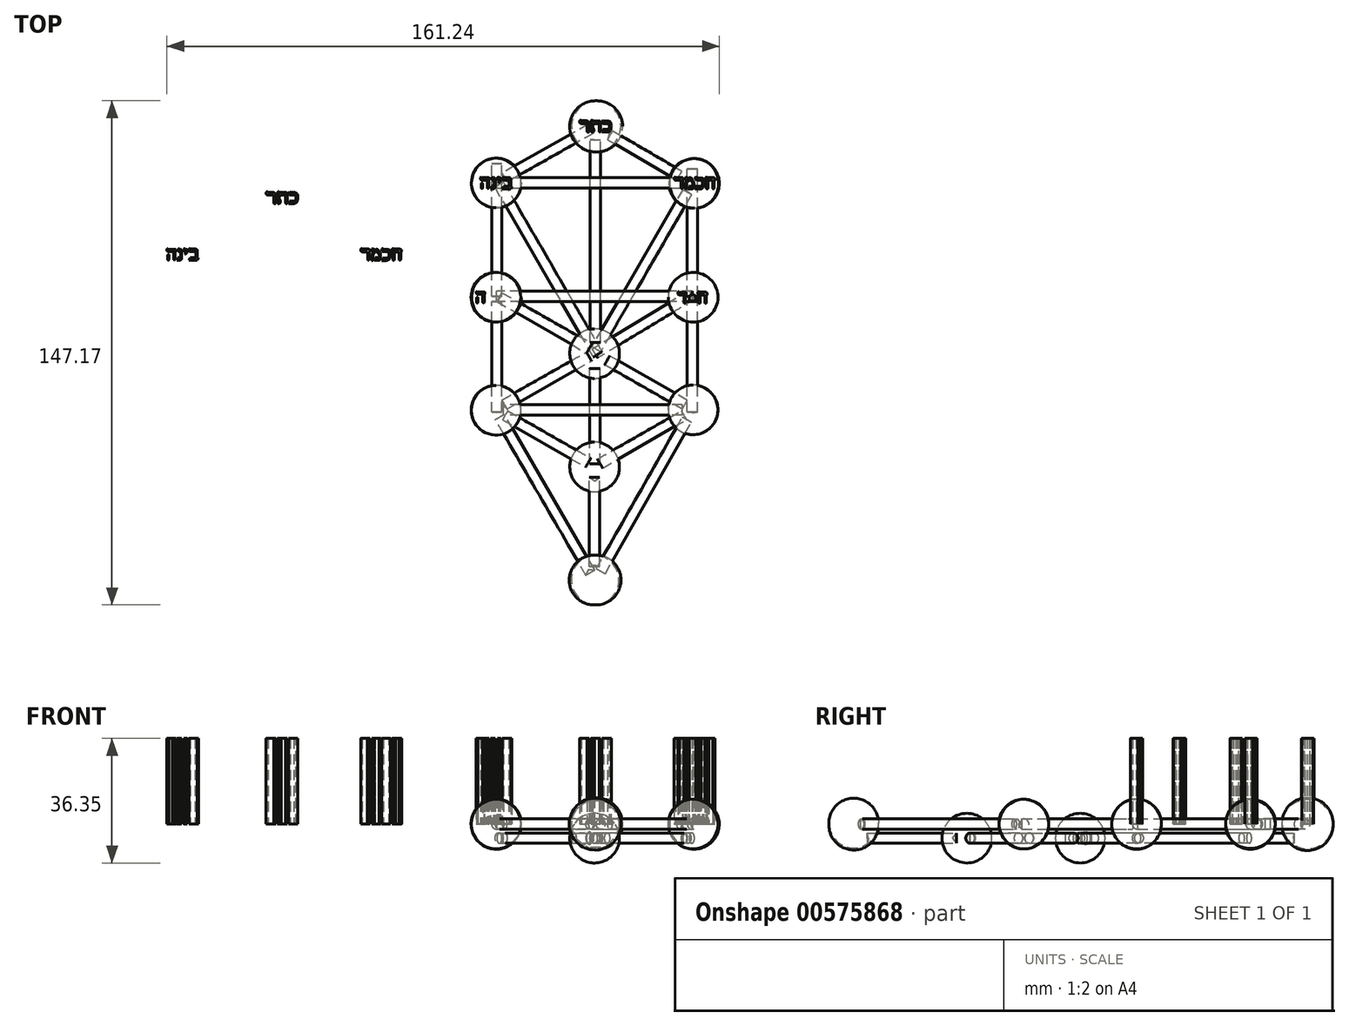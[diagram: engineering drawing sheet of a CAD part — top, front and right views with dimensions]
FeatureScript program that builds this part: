
annotation { "Feature Type Name" : "Feature", "Feature Type Description" : "" }
export const myFeature = defineFeature(function(context is Context, id is Id, definition is map)
    precondition{}
    {
        {
            var Q0;
            Q0=qCreatedBy(makeId("Top.planeOp"),FACE);
            var sketch = newSketch(context, id + "F0", { "sketchPlane" : qUnion([Q0])});
            skArc(sketch, "E0", {"start": v(-29.22, -23.77) * mm, "mid": v(-22, -15.76) * mm, "end": v(-30.74, -9.44) * mm});
            skArc(sketch, "E1", {"start": v(-30.68, 9.37) * mm, "mid": v(-21.85, 16.42) * mm, "end": v(-30.63, 23.53) * mm});
            skArc(sketch, "E2", {"start": v(28.3, -9.18) * mm, "mid": v(21.06, -16.43) * mm, "end": v(28.3, -23.68) * mm});
            skArc(sketch, "E3", {"start": v(-0.3, -73.36) * mm, "mid": v(7.25, -66.12) * mm, "end": v(-0.3, -58.88) * mm});
            skArc(sketch, "E4", {"start": v(21.05, 16.45) * mm, "mid": v(28.3, 9.2) * mm, "end": v(35.55, 16.45) * mm});
            skArc(sketch, "E5", {"start": v(28.6, 56.94) * mm, "mid": v(21.43, 49.7) * mm, "end": v(28.6, 42.44) * mm});
            skArc(sketch, "E6", {"start": v(-30.57, 42.7) * mm, "mid": v(-21.95, 49.1) * mm, "end": v(-29.15, 57.06) * mm});
            skLineSegment(sketch, "E7", {"start": v(-30.44, -92.86) * mm, "end": v(-28.9, -92.86) * mm});
            skPoint(sketch, "E8.end.orphan", {"position": v(28.3, -15.3) * mm});
            skPoint(sketch, "E9.start.orphan", {"position": v(-2.21, -66.12) * mm});
            skPoint(sketch, "E10.orphan", {"position": v(4.16, -62.34) * mm});
            skPoint(sketch, "E11.orphan", {"position": v(26.56, 15.81) * mm});
            skLineSegment(sketch, "E12", {"start": v(-29.22, -9.27) * mm, "end": v(-29.22, -23.77) * mm});
            skLineSegment(sketch, "E13", {"start": v(28.3, -9.18) * mm, "end": v(28.3, -23.68) * mm});
            skLineSegment(sketch, "E14", {"start": v(-29.12, 23.7) * mm, "end": v(-29.25, 9.2) * mm});
            skLineSegment(sketch, "E15", {"start": v(-29.15, 42.56) * mm, "end": v(-29.15, 57.06) * mm});
            skLineSegment(sketch, "E16", {"start": v(-0.3, -58.88) * mm, "end": v(-0.3, -73.36) * mm});
            skLineSegment(sketch, "E17", {"start": v(21.05, 16.45) * mm, "end": v(35.55, 16.45) * mm});
            skArc(sketch, "E18.trimOffspring", {"start": v(28.6, 23.7) * mm, "mid": v(27.57, 23.66) * mm, "end": v(26.56, 23.49) * mm});
            skLineSegment(sketch, "E19", {"start": v(28.6, 42.44) * mm, "end": v(28.6, 56.94) * mm});
            skArc(sketch, "E20.trimOffspring", {"start": v(5.17, 61.31) * mm, "mid": v(5.76, 62) * mm, "end": v(6.26, 62.75) * mm});
            skArc(sketch, "E21", {"start": v(5.2, 61.29) * mm, "mid": v(5.78, 61.99) * mm, "end": v(6.26, 62.75) * mm});
            skLineSegment(sketch, "E22", {"start": v(0, 66.4) * mm, "end": v(0, 73.8) * mm});
            skLineSegment(sketch, "E23", {"start": v(0, 73.8) * mm, "end": v(0, 58.9) * mm});
            skArc(sketch, "E24.trimOffspring", {"start": v(0, 73.8) * mm, "mid": v(-7.71, 66.35) * mm, "end": v(0, 58.9) * mm});
            skSolve(sketch);
        }
        {
            var Q0;
            {var subQ5=sQuery(id+"F0.wireOp",EDGE,"E12");Q0=makeQuery(id+"F0.imprint","IMPRINT",FACE,{"disambiguationData":[TD([[makeQuery(id+"F0.imprint","IMPRINT",EDGE,{"derivedFrom":subQ5}),1.0]])]});}
            var Q1;
            Q1=sQuery(id+"F0.wireOp",EDGE,"E12");
            revolve(context, id + "F1", {"entities" : qUnion([Q0]), "axis" : qUnion([Q1]), "revolveType" : RevolveType.FULL});
        }
        {
            var Q0;
            {var subQ5=sQuery(id+"F0.wireOp",EDGE,"E13");Q0=makeQuery(id+"F0.imprint","IMPRINT",FACE,{"disambiguationData":[TD([[makeQuery(id+"F0.imprint","IMPRINT",EDGE,{"derivedFrom":subQ5}),-1.0]])]});}
            var Q1;
            Q1=sQuery(id+"F0.wireOp",EDGE,"E13");
            revolve(context, id + "F2", {"entities" : qUnion([Q0]), "axis" : qUnion([Q1]), "revolveType" : RevolveType.FULL});
        }
        {
            var Q0;
            {var subQ0=sQuery(id+"F0.wireOp",EDGE,"E14");Q0=makeQuery(id+"F0.imprint","IMPRINT",FACE,{"disambiguationData":[TD([[makeQuery(id+"F0.imprint","IMPRINT",EDGE,{"derivedFrom":subQ0}),1.0]])]});}
            var Q1;
            Q1=sQuery(id+"F0.wireOp",EDGE,"E14");
            revolve(context, id + "F3", {"entities" : qUnion([Q0]), "axis" : qUnion([Q1]), "revolveType" : RevolveType.FULL});
        }
        {
            var Q0;
            {var subQ5=sQuery(id+"F0.wireOp",EDGE,"E15");Q0=makeQuery(id+"F0.imprint","IMPRINT",FACE,{"disambiguationData":[TD([[makeQuery(id+"F0.imprint","IMPRINT",EDGE,{"derivedFrom":subQ5}),-1.0]])]});}
            var Q1;
            Q1=sQuery(id+"F0.wireOp",EDGE,"E15");
            revolve(context, id + "F4", {"entities" : qUnion([Q0]), "axis" : qUnion([Q1]), "revolveType" : RevolveType.FULL});
        }
        {
            var Q0;
            {var subQ0=sQuery(id+"F0.wireOp",EDGE,"E16");Q0=makeQuery(id+"F0.imprint","IMPRINT",FACE,{"disambiguationData":[TD([[makeQuery(id+"F0.imprint","IMPRINT",EDGE,{"derivedFrom":subQ0}),1.0]])]});}
            var Q1;
            Q1=sQuery(id+"F0.wireOp",EDGE,"E16");
            revolve(context, id + "F5", {"entities" : qUnion([Q0]), "axis" : qUnion([Q1]), "revolveType" : RevolveType.FULL});
        }
        {
            var Q0;
            {var subQ0=sQuery(id+"F0.wireOp",EDGE,"E17");Q0=makeQuery(id+"F0.imprint","IMPRINT",FACE,{"disambiguationData":[TD([[makeQuery(id+"F0.imprint","IMPRINT",EDGE,{"derivedFrom":subQ0}),-1.0]])]});}
            var Q1;
            Q1=sQuery(id+"F0.wireOp",EDGE,"E17");
            revolve(context, id + "F6", {"entities" : qUnion([Q0]), "axis" : qUnion([Q1]), "revolveType" : RevolveType.FULL});
        }
        {
            var Q0;
            {var subQ4=sQuery(id+"F0.wireOp",EDGE,"E19");Q0=makeQuery(id+"F0.imprint","IMPRINT",FACE,{"disambiguationData":[TD([[makeQuery(id+"F0.imprint","IMPRINT",EDGE,{"derivedFrom":subQ4}),1.0]])]});}
            var Q1;
            Q1=sQuery(id+"F0.wireOp",EDGE,"E19");
            revolve(context, id + "F7", {"entities" : qUnion([Q0]), "axis" : qUnion([Q1]), "revolveType" : RevolveType.FULL});
        }
        {
            var Q0;
            {var subQ0=sQuery(id+"F0.wireOp",EDGE,"E24.trimOffspring");var subQ1=sQuery(id+"F0.wireOp",EDGE,"E23");var subQ2=makeQuery(id+"F0.imprint","INTERSECT",VERTEX,{"disambiguationData":[OD(0.0)],"derivedFrom":[subQ1,subQ0]});Q0=makeQuery(id+"F0.imprint","IMPRINT",FACE,{"disambiguationData":[TD([[makeQuery(id+"F0.imprint","IMPRINT",EDGE,{"disambiguationData":[TD([[subQ2,-1.0]])],"derivedFrom":subQ1}),-1.0]])]});}
            var Q1;
            Q1=sQuery(id+"F0.wireOp",EDGE,"E23");
            revolve(context, id + "F8", {"entities" : qUnion([Q0]), "axis" : qUnion([Q1]), "revolveType" : RevolveType.FULL});
        }
        {
            var Q0;
            Q0=qCreatedBy(makeId("Top.planeOp"),FACE);
            cPlane(context, id + "F9", {"entities" : qUnion([Q0]), "cplaneType" : CPlaneType.OFFSET, "offset" : 4.1 * mm, "oppositeDirection" : true, "width" : 150 * mm, "height" : 150 * mm});
        }
        {
            var Q0;
            Q0=qCreatedBy(id+"F9.planeOp",FACE);
            var sketch = newSketch(context, id + "F10", { "sketchPlane" : qUnion([Q0])});
            skLineSegment(sketch, "E25", {"start": v(-0.45, -60.42) * mm, "end": v(-1.91, -60.42) * mm});
            skArc(sketch, "E26", {"start": v(-0.45, -7.25) * mm, "mid": v(6.8, 0) * mm, "end": v(-0.45, 7.25) * mm});
            skLineSegment(sketch, "E27", {"start": v(-0.45, 0) * mm, "end": v(-0.45, -7.25) * mm});
            skLineSegment(sketch, "E28", {"start": v(-0.45, -7.25) * mm, "end": v(-0.45, 7.25) * mm});
            skLineSegment(sketch, "E29", {"start": v(-0.45, -25.83) * mm, "end": v(-0.45, -40.33) * mm});
            skArc(sketch, "E30", {"start": v(-0.45, -40.33) * mm, "mid": v(6.8, -33.08) * mm, "end": v(-0.45, -25.83) * mm});
            skSolve(sketch);
        }
        {
            var Q0;
            Q0=makeQuery(id+"F10.imprint","IMPRINT",FACE,{"disambiguationData":[TD([[makeQuery(id+"F10.imprint","IMPRINT",EDGE,{"derivedFrom":sQuery(id+"F10.wireOp",EDGE,"E29")}),1.0]])]});
            var Q1;
            {var subQ0=sQuery(id+"F10.wireOp",EDGE,"E26");Q1=makeQuery(id+"F10.imprint","IMPRINT",FACE,{"disambiguationData":[TD([[makeQuery(id+"F10.imprint","IMPRINT",EDGE,{"derivedFrom":subQ0}),1.0]])]});}
            var Q2;
            Q2=sQuery(id+"F10.wireOp",EDGE,"E29");
            revolve(context, id + "F11", {"entities" : qUnion([Q0, Q1]), "axis" : qUnion([Q2]), "revolveType" : RevolveType.FULL});
        }
        {
            var Q0;
            Q0=qCreatedBy(id+"F9.planeOp",FACE);
            var sketch = newSketch(context, id + "F12", { "sketchPlane" : qUnion([Q0])});
            skLineSegment(sketch, "E31", {"start": v(-1.97, -62.21) * mm, "end": v(-1.97, -36.17) * mm});
            skLineSegment(sketch, "E32", {"start": v(-0.47, -37.24) * mm, "end": v(-0.47, -61.75) * mm});
            skLineSegment(sketch, "E33", {"start": v(-1.97, -36.17) * mm, "end": v(-0.47, -37.24) * mm});
            skLineSegment(sketch, "E34", {"start": v(-1.97, -62.21) * mm, "end": v(-0.47, -61.75) * mm});
            skLineSegment(sketch, "E35", {"start": v(1.87, -33.42) * mm, "end": v(26.38, -19.33) * mm});
            skLineSegment(sketch, "E36", {"start": v(26.38, -19.33) * mm, "end": v(25.63, -18.03) * mm});
            skLineSegment(sketch, "E37", {"start": v(25.63, -18.03) * mm, "end": v(1.2, -32.08) * mm});
            skLineSegment(sketch, "E38", {"start": v(1.2, -32.08) * mm, "end": v(1.87, -33.42) * mm});
            skPoint(sketch, "E39", {"position": v(-2.06, -12.41) * mm});
            skLineSegment(sketch, "E40", {"start": v(-1.91, -26.94) * mm, "end": v(-1.91, -4.4) * mm});
            skLineSegment(sketch, "E41", {"start": v(-1.91, -4.4) * mm, "end": v(-0.41, -4.4) * mm});
            skLineSegment(sketch, "E42", {"start": v(-0.41, -4.4) * mm, "end": v(-0.41, -26.9) * mm});
            skLineSegment(sketch, "E43", {"start": v(2.46, -3.24) * mm, "end": v(3.2, -1.94) * mm});
            skLineSegment(sketch, "E44", {"start": v(-25.22, 13.02) * mm, "end": v(-7.19, 2.78) * mm});
            skLineSegment(sketch, "E45", {"start": v(-6.45, 4.09) * mm, "end": v(-24.48, 14.32) * mm});
            skLineSegment(sketch, "E46", {"start": v(5.2, 3.36) * mm, "end": v(23.09, 14.2) * mm});
            skLineSegment(sketch, "E47", {"start": v(20.38, 14.32) * mm, "end": v(4.35, 4.6) * mm});
            skLineSegment(sketch, "E48", {"start": v(-1.78, 62.44) * mm, "end": v(-1.78, 3.22) * mm});
            skLineSegment(sketch, "E49", {"start": v(-0.28, 62.35) * mm, "end": v(-0.28, 3.22) * mm});
            skLineSegment(sketch, "E50", {"start": v(-1.78, 62.44) * mm, "end": v(-0.28, 62.35) * mm});
            skLineSegment(sketch, "E51", {"start": v(-0.28, 3.22) * mm, "end": v(-1.78, 3.22) * mm});
            skLineSegment(sketch, "E52", {"start": v(-27.33, -19.33) * mm, "end": v(-6.6, -31.15) * mm});
            skLineSegment(sketch, "E53", {"start": v(-5.84, -29.86) * mm, "end": v(-26.58, -18.03) * mm});
            skLineSegment(sketch, "E54", {"start": v(-26.58, -18.03) * mm, "end": v(-27.33, -19.33) * mm});
            skLineSegment(sketch, "E55", {"start": v(2.46, -3.24) * mm, "end": v(25.12, -16.2) * mm});
            skLineSegment(sketch, "E56", {"start": v(25.12, -16.2) * mm, "end": v(25.86, -14.9) * mm});
            skLineSegment(sketch, "E57", {"start": v(3.2, -1.94) * mm, "end": v(25.86, -14.9) * mm});
            skLineSegment(sketch, "E58", {"start": v(-5.04, -4.26) * mm, "end": v(-26, -16.2) * mm});
            skLineSegment(sketch, "E59", {"start": v(-5.78, -2.96) * mm, "end": v(-27.1, -15.1) * mm});
            skLineSegment(sketch, "E60", {"start": v(-27.1, -15.1) * mm, "end": v(-26, -16.2) * mm});
            skLineSegment(sketch, "E61", {"start": v(-5.04, -4.26) * mm, "end": v(-1.33, -2.16) * mm});
            skLineSegment(sketch, "E62", {"start": v(-5.78, -2.96) * mm, "end": v(-1.97, -0.8) * mm});
            skLineSegment(sketch, "E63", {"start": v(-1.97, -0.8) * mm, "end": v(-1.33, -2.16) * mm});
            skLineSegment(sketch, "E64", {"start": v(-25.22, 13.02) * mm, "end": v(-29, 15.16) * mm});
            skLineSegment(sketch, "E65", {"start": v(-24.48, 14.32) * mm, "end": v(-28.06, 16.35) * mm});
            skLineSegment(sketch, "E66", {"start": v(-29, 15.16) * mm, "end": v(-28.06, 16.35) * mm});
            skLineSegment(sketch, "E67", {"start": v(-7.19, 2.78) * mm, "end": v(-2.86, 0) * mm});
            skLineSegment(sketch, "E68", {"start": v(-6.45, 4.09) * mm, "end": v(-1.93, 1.53) * mm});
            skLineSegment(sketch, "E69", {"start": v(-1.93, 1.53) * mm, "end": v(-2.86, 0) * mm});
            skLineSegment(sketch, "E70", {"start": v(5.2, 3.36) * mm, "end": v(27.9, 17.13) * mm});
            skLineSegment(sketch, "E71", {"start": v(20.38, 14.32) * mm, "end": v(27.15, 18.42) * mm});
            skLineSegment(sketch, "E72", {"start": v(27.15, 18.42) * mm, "end": v(27.9, 17.13) * mm});
            skLineSegment(sketch, "E73", {"start": v(5.2, 3.36) * mm, "end": v(-0.35, 0) * mm});
            skLineSegment(sketch, "E74", {"start": v(-0.35, 0) * mm, "end": v(-1.13, 1.28) * mm});
            skLineSegment(sketch, "E75", {"start": v(4.35, 4.6) * mm, "end": v(-1.13, 1.28) * mm});
            skLineSegment(sketch, "E76", {"start": v(-1.91, -26.94) * mm, "end": v(-1.91, -32.18) * mm});
            skLineSegment(sketch, "E77", {"start": v(-0.41, -26.9) * mm, "end": v(-0.41, -32.14) * mm});
            skLineSegment(sketch, "E78", {"start": v(-0.41, -32.14) * mm, "end": v(-1.91, -32.18) * mm});
            skLineSegment(sketch, "E79", {"start": v(-6.6, -31.15) * mm, "end": v(-3.06, -33.17) * mm});
            skLineSegment(sketch, "E80", {"start": v(-3.06, -33.17) * mm, "end": v(-2.32, -31.86) * mm});
            skLineSegment(sketch, "E81", {"start": v(-5.84, -29.86) * mm, "end": v(-2.32, -31.86) * mm});
            skLineSegment(sketch, "E82", {"start": v(-5.3, 0) * mm, "end": v(4.25, 0) * mm});
            skSolve(sketch);
        }
        {
            var Q0;
            Q0=makeQuery(id+"F12.imprint","IMPRINT",FACE,{"disambiguationData":[TD([[makeQuery(id+"F12.imprint","IMPRINT",EDGE,{"derivedFrom":sQuery(id+"F12.wireOp",EDGE,"E58")}),-1.0]])]});
            var Q1;
            Q1=sQuery(id+"F12.wireOp",EDGE,"E59");
            revolve(context, id + "F13", {"entities" : qUnion([Q0]), "axis" : qUnion([Q1]), "revolveType" : RevolveType.FULL});
        }
        {
            var Q0;
            Q0=makeQuery(id+"F12.imprint","IMPRINT",FACE,{"disambiguationData":[TD([[makeQuery(id+"F12.imprint","IMPRINT",EDGE,{"derivedFrom":sQuery(id+"F12.wireOp",EDGE,"E47")}),1.0]])]});
            var Q1;
            Q1=sQuery(id+"F12.wireOp",EDGE,"E46");
            revolve(context, id + "F14", {"entities" : qUnion([Q0]), "axis" : qUnion([Q1]), "revolveType" : RevolveType.FULL});
        }
        {
            var Q0;
            Q0=makeQuery(id+"F12.imprint","IMPRINT",FACE,{"disambiguationData":[TD([[makeQuery(id+"F12.imprint","IMPRINT",EDGE,{"derivedFrom":sQuery(id+"F12.wireOp",EDGE,"E44")}),1.0]])]});
            var Q1;
            Q1=sQuery(id+"F12.wireOp",EDGE,"E45");
            revolve(context, id + "F15", {"entities" : qUnion([Q0]), "axis" : qUnion([Q1]), "revolveType" : RevolveType.FULL});
        }
        {
            var Q0;
            Q0=makeQuery(id+"F12.imprint","IMPRINT",FACE,{"disambiguationData":[TD([[makeQuery(id+"F12.imprint","IMPRINT",EDGE,{"derivedFrom":sQuery(id+"F12.wireOp",EDGE,"E43")}),-1.0]])]});
            var Q1;
            Q1=sQuery(id+"F12.wireOp",EDGE,"E57");
            revolve(context, id + "F16", {"entities" : qUnion([Q0]), "axis" : qUnion([Q1]), "revolveType" : RevolveType.FULL});
        }
        {
            var Q0;
            Q0=makeQuery(id+"F12.imprint","IMPRINT",FACE,{"disambiguationData":[TD([[makeQuery(id+"F12.imprint","IMPRINT",EDGE,{"derivedFrom":sQuery(id+"F12.wireOp",EDGE,"E48")}),1.0]])]});
            var Q1;
            Q1=sQuery(id+"F12.wireOp",EDGE,"E49");
            revolve(context, id + "F17", {"entities" : qUnion([Q0]), "axis" : qUnion([Q1]), "revolveType" : RevolveType.FULL});
        }
        {
            var Q0;
            Q0=makeQuery(id+"F12.imprint","IMPRINT",FACE,{"disambiguationData":[TD([[makeQuery(id+"F12.imprint","IMPRINT",EDGE,{"derivedFrom":sQuery(id+"F12.wireOp",EDGE,"E52")}),1.0]])]});
            var Q1;
            Q1=sQuery(id+"F12.wireOp",EDGE,"E53");
            revolve(context, id + "F18", {"entities" : qUnion([Q0]), "axis" : qUnion([Q1]), "revolveType" : RevolveType.FULL});
        }
        {
            var Q0;
            Q0=makeQuery(id+"F12.imprint","IMPRINT",FACE,{"disambiguationData":[TD([[makeQuery(id+"F12.imprint","IMPRINT",EDGE,{"derivedFrom":sQuery(id+"F12.wireOp",EDGE,"E35")}),1.0]])]});
            var Q1;
            Q1=sQuery(id+"F12.wireOp",EDGE,"E37");
            revolve(context, id + "F19", {"entities" : qUnion([Q0]), "axis" : qUnion([Q1]), "revolveType" : RevolveType.FULL});
        }
        {
            var Q0;
            Q0=makeQuery(id+"F12.imprint","IMPRINT",FACE,{"disambiguationData":[TD([[makeQuery(id+"F12.imprint","IMPRINT",EDGE,{"derivedFrom":sQuery(id+"F12.wireOp",EDGE,"E40")}),-1.0]])]});
            var Q1;
            Q1=sQuery(id+"F12.wireOp",EDGE,"E42");
            revolve(context, id + "F20", {"entities" : qUnion([Q0]), "axis" : qUnion([Q1]), "revolveType" : RevolveType.FULL});
        }
        {
            var Q0;
            Q0=makeQuery(id+"F12.imprint","IMPRINT",FACE,{"disambiguationData":[TD([[makeQuery(id+"F12.imprint","IMPRINT",EDGE,{"derivedFrom":sQuery(id+"F12.wireOp",EDGE,"E31")}),-1.0]])]});
            var Q1;
            Q1=sQuery(id+"F12.wireOp",EDGE,"E32");
            revolve(context, id + "F21", {"entities" : qUnion([Q0]), "axis" : qUnion([Q1]), "revolveType" : RevolveType.FULL});
        }
        {
            var Q0;
            Q0=qCreatedBy(id+"F9.planeOp",FACE);
            var sketch = newSketch(context, id + "F22", { "sketchPlane" : qUnion([Q0])});
            skLineSegment(sketch, "E83", {"start": v(-29.65, 48.54) * mm, "end": v(-0.85, -1) * mm});
            skLineSegment(sketch, "E84", {"start": v(-0.85, -1) * mm, "end": v(0.44, -0.24) * mm});
            skLineSegment(sketch, "E85", {"start": v(0.44, -0.24) * mm, "end": v(-28.42, 49.41) * mm});
            skLineSegment(sketch, "E86", {"start": v(-28.42, 49.41) * mm, "end": v(-29.65, 48.54) * mm});
            skLineSegment(sketch, "E87", {"start": v(27.83, 46.38) * mm, "end": v(1.3, 0.51) * mm});
            skLineSegment(sketch, "E88", {"start": v(1.3, 0.51) * mm, "end": v(0, 1.27) * mm});
            skLineSegment(sketch, "E89", {"start": v(0, 1.27) * mm, "end": v(26.66, 47.36) * mm});
            skLineSegment(sketch, "E90", {"start": v(26.66, 47.36) * mm, "end": v(27.83, 46.38) * mm});
            skSolve(sketch);
        }
        {
            var Q0;
            Q0=makeQuery(id+"F22.imprint","IMPRINT",FACE,{"disambiguationData":[TD([[makeQuery(id+"F22.imprint","IMPRINT",EDGE,{"derivedFrom":sQuery(id+"F22.wireOp",EDGE,"E83")}),1.0]])]});
            var Q1;
            Q1=sQuery(id+"F22.wireOp",EDGE,"E85");
            revolve(context, id + "F23", {"entities" : qUnion([Q0]), "axis" : qUnion([Q1]), "revolveType" : RevolveType.FULL});
        }
        {
            var Q0;
            Q0=makeQuery(id+"F22.imprint","IMPRINT",FACE,{"disambiguationData":[TD([[makeQuery(id+"F22.imprint","IMPRINT",EDGE,{"derivedFrom":sQuery(id+"F22.wireOp",EDGE,"E87")}),-1.0]])]});
            var Q1;
            Q1=sQuery(id+"F22.wireOp",EDGE,"E89");
            revolve(context, id + "F24", {"entities" : qUnion([Q0]), "axis" : qUnion([Q1]), "revolveType" : RevolveType.FULL});
        }
        {
            var Q0;
            Q0=qCreatedBy(makeId("Top.planeOp"),FACE);
            var sketch = newSketch(context, id + "F25", { "sketchPlane" : qUnion([Q0])});
            skLineSegment(sketch, "E91", {"start": v(-30.53, -17.09) * mm, "end": v(-30.53, 47.6) * mm});
            skLineSegment(sketch, "E92", {"start": v(-29.03, 47.6) * mm, "end": v(-29.03, -17.23) * mm});
            skLineSegment(sketch, "E93", {"start": v(-29.03, -17.23) * mm, "end": v(-30.53, -17.09) * mm});
            skLineSegment(sketch, "E94", {"start": v(29.58, 47.6) * mm, "end": v(29.58, -17.09) * mm});
            skLineSegment(sketch, "E95", {"start": v(28.08, 47.6) * mm, "end": v(28.08, -17.28) * mm});
            skLineSegment(sketch, "E96", {"start": v(28.08, -17.28) * mm, "end": v(29.58, -17.09) * mm});
            skLineSegment(sketch, "E97", {"start": v(-30.53, 15.25) * mm, "end": v(29.58, 15.25) * mm});
            skLineSegment(sketch, "E98", {"start": v(-30.53, 16.75) * mm, "end": v(29.58, 16.75) * mm});
            skLineSegment(sketch, "E99", {"start": v(25.1, -17.95) * mm, "end": v(-27.07, -17.95) * mm});
            skLineSegment(sketch, "E100", {"start": v(-29.03, -17.95) * mm, "end": v(-29.03, -16.45) * mm});
            skLineSegment(sketch, "E101", {"start": v(-27.07, -16.45) * mm, "end": v(25.1, -16.45) * mm});
            skLineSegment(sketch, "E102", {"start": v(-30.53, 47.6) * mm, "end": v(-30.53, 55.48) * mm});
            skLineSegment(sketch, "E103", {"start": v(-30.53, 55.48) * mm, "end": v(-29.03, 55.48) * mm});
            skLineSegment(sketch, "E104", {"start": v(-29.03, 47.6) * mm, "end": v(-29.03, 55.48) * mm});
            skLineSegment(sketch, "E105", {"start": v(28.08, 47.6) * mm, "end": v(28.08, 53.95) * mm});
            skLineSegment(sketch, "E106", {"start": v(29.58, 47.6) * mm, "end": v(29.58, 53.95) * mm});
            skLineSegment(sketch, "E107", {"start": v(28.08, 53.95) * mm, "end": v(29.58, 53.95) * mm});
            skPoint(sketch, "E108.orphan", {"position": v(29.58, 54.22) * mm});
            skLineSegment(sketch, "E109", {"start": v(-29.03, 48.35) * mm, "end": v(28.08, 48.35) * mm});
            skLineSegment(sketch, "E110", {"start": v(28.08, 48.35) * mm, "end": v(28.08, 49.85) * mm});
            skLineSegment(sketch, "E111", {"start": v(28.08, 49.85) * mm, "end": v(-29.03, 49.85) * mm});
            skLineSegment(sketch, "E112", {"start": v(-27.43, 52.75) * mm, "end": v(-2.25, 67) * mm});
            skLineSegment(sketch, "E113", {"start": v(-27.43, 52.75) * mm, "end": v(-26.7, 51.45) * mm});
            skLineSegment(sketch, "E114", {"start": v(-26.7, 51.45) * mm, "end": v(-1.5, 65.7) * mm});
            skLineSegment(sketch, "E115", {"start": v(-1.5, 65.7) * mm, "end": v(-2.25, 67) * mm});
            skPoint(sketch, "E116.start.orphan", {"position": v(0, 68.28) * mm});
            skLineSegment(sketch, "E117", {"start": v(25, 53.28) * mm, "end": v(4.78, 65.04) * mm});
            skLineSegment(sketch, "E118", {"start": v(25, 53.28) * mm, "end": v(24.25, 51.98) * mm});
            skLineSegment(sketch, "E119", {"start": v(24.25, 51.98) * mm, "end": v(3.71, 63.93) * mm});
            skLineSegment(sketch, "E120", {"start": v(3.71, 63.93) * mm, "end": v(4.78, 65.04) * mm});
            skLineSegment(sketch, "E121", {"start": v(-27.07, -16.45) * mm, "end": v(-27.07, -17.95) * mm});
            skLineSegment(sketch, "E122", {"start": v(25.1, -16.45) * mm, "end": v(25.1, -17.95) * mm});
            skLineSegment(sketch, "E123", {"start": v(-29.44, -19.28) * mm, "end": v(-3.03, -64.7) * mm});
            skLineSegment(sketch, "E124", {"start": v(-29.44, -19.28) * mm, "end": v(-28.14, -18.52) * mm});
            skLineSegment(sketch, "E125", {"start": v(-28.14, -18.52) * mm, "end": v(-2.3, -62.99) * mm});
            skLineSegment(sketch, "E126", {"start": v(-2.3, -62.99) * mm, "end": v(-3.03, -64.7) * mm});
            skLineSegment(sketch, "E127", {"start": v(0, -62.78) * mm, "end": v(25.18, -18.52) * mm});
            skLineSegment(sketch, "E128", {"start": v(26.48, -19.27) * mm, "end": v(1.3, -63.52) * mm});
            skLineSegment(sketch, "E129", {"start": v(0, -62.78) * mm, "end": v(1.3, -63.52) * mm});
            skLineSegment(sketch, "E130", {"start": v(25.18, -18.52) * mm, "end": v(26.48, -19.27) * mm});
            skSolve(sketch);
        }
        {
            var Q0;
            Q0=makeQuery(id+"F25.imprint","IMPRINT",FACE,{"disambiguationData":[TD([[makeQuery(id+"F25.imprint","IMPRINT",EDGE,{"derivedFrom":sQuery(id+"F25.wireOp",EDGE,"E112")}),-1.0]])]});
            var Q1;
            Q1=sQuery(id+"F25.wireOp",EDGE,"E114");
            revolve(context, id + "F26", {"entities" : qUnion([Q0]), "axis" : qUnion([Q1]), "revolveType" : RevolveType.FULL});
        }
        {
            var Q0;
            Q0=makeQuery(id+"F25.imprint","IMPRINT",FACE,{"disambiguationData":[TD([[makeQuery(id+"F25.imprint","IMPRINT",EDGE,{"derivedFrom":sQuery(id+"F25.wireOp",EDGE,"E117")}),1.0]])]});
            var Q1;
            Q1=sQuery(id+"F25.wireOp",EDGE,"E119");
            revolve(context, id + "F27", {"entities" : qUnion([Q0]), "axis" : qUnion([Q1]), "revolveType" : RevolveType.FULL});
        }
        {
            var Q0;
            {var subQ0=sQuery(id+"F25.wireOp",EDGE,"E109");Q0=makeQuery(id+"F25.imprint","IMPRINT",FACE,{"disambiguationData":[TD([[makeQuery(id+"F25.imprint","IMPRINT",EDGE,{"derivedFrom":subQ0}),1.0]])]});}
            var Q1;
            Q1=sQuery(id+"F25.wireOp",EDGE,"E111");
            revolve(context, id + "F28", {"entities" : qUnion([Q0]), "axis" : qUnion([Q1]), "revolveType" : RevolveType.FULL});
        }
        {
            var Q0;
            {var subQ0=sQuery(id+"F25.wireOp",EDGE,"E98");var subQ1=sQuery(id+"F25.wireOp",EDGE,"E92");var subQ2=makeQuery(id+"F25.imprint","INTERSECT",VERTEX,{"derivedFrom":[subQ1,subQ0]});Q0=makeQuery(id+"F25.imprint","IMPRINT",FACE,{"disambiguationData":[TD([[makeQuery(id+"F25.imprint","IMPRINT",EDGE,{"disambiguationData":[TD([[subQ2,-1.0]])],"derivedFrom":subQ1}),1.0]])]});}
            var Q1;
            Q1=sQuery(id+"F25.wireOp",EDGE,"E98");
            revolve(context, id + "F29", {"entities" : qUnion([Q0]), "axis" : qUnion([Q1]), "revolveType" : RevolveType.FULL});
        }
        {
            var Q0;
            Q0=makeQuery(id+"F25.imprint","IMPRINT",FACE,{"disambiguationData":[TD([[makeQuery(id+"F25.imprint","IMPRINT",EDGE,{"derivedFrom":sQuery(id+"F25.wireOp",EDGE,"E99")}),-1.0]])]});
            var Q1;
            Q1=sQuery(id+"F25.wireOp",EDGE,"E101");
            revolve(context, id + "F30", {"entities" : qUnion([Q0]), "axis" : qUnion([Q1]), "revolveType" : RevolveType.FULL});
        }
        {
            var Q0;
            {var subQ0=sQuery(id+"F25.wireOp",EDGE,"E102");Q0=makeQuery(id+"F25.imprint","IMPRINT",FACE,{"disambiguationData":[TD([[makeQuery(id+"F25.imprint","IMPRINT",EDGE,{"derivedFrom":subQ0}),-1.0]])]});}
            var Q1;
            Q1=sQuery(id+"F25.wireOp",EDGE,"E92");
            revolve(context, id + "F31", {"entities" : qUnion([Q0]), "axis" : qUnion([Q1]), "revolveType" : RevolveType.FULL});
        }
        {
            var Q0;
            {var subQ5=sQuery(id+"F25.wireOp",EDGE,"E93");Q0=makeQuery(id+"F25.imprint","IMPRINT",FACE,{"disambiguationData":[TD([[makeQuery(id+"F25.imprint","IMPRINT",EDGE,{"derivedFrom":subQ5}),-1.0]])]});}
            var Q1;
            Q1=sQuery(id+"F25.wireOp",EDGE,"E92");
            revolve(context, id + "F32", {"entities" : qUnion([Q0]), "axis" : qUnion([Q1]), "revolveType" : RevolveType.FULL});
        }
        {
            var Q0;
            {var subQ8=sQuery(id+"F25.wireOp",EDGE,"E106");Q0=makeQuery(id+"F25.imprint","IMPRINT",FACE,{"disambiguationData":[TD([[makeQuery(id+"F25.imprint","IMPRINT",EDGE,{"derivedFrom":subQ8}),1.0]])]});}
            var Q1;
            Q1=sQuery(id+"F25.wireOp",EDGE,"E95");
            revolve(context, id + "F33", {"entities" : qUnion([Q0]), "axis" : qUnion([Q1]), "revolveType" : RevolveType.FULL});
        }
        {
            var Q0;
            {var subQ0=sQuery(id+"F25.wireOp",EDGE,"E96");Q0=makeQuery(id+"F25.imprint","IMPRINT",FACE,{"disambiguationData":[TD([[makeQuery(id+"F25.imprint","IMPRINT",EDGE,{"derivedFrom":subQ0}),1.0]])]});}
            var Q1;
            Q1=sQuery(id+"F25.wireOp",EDGE,"E95");
            revolve(context, id + "F34", {"entities" : qUnion([Q0]), "axis" : qUnion([Q1]), "revolveType" : RevolveType.FULL});
        }
        {
            var Q0;
            Q0=makeQuery(id+"F25.imprint","IMPRINT",FACE,{"disambiguationData":[TD([[makeQuery(id+"F25.imprint","IMPRINT",EDGE,{"derivedFrom":sQuery(id+"F25.wireOp",EDGE,"E123")}),1.0]])]});
            var Q1;
            Q1=sQuery(id+"F25.wireOp",EDGE,"E125");
            revolve(context, id + "F35", {"entities" : qUnion([Q0]), "axis" : qUnion([Q1]), "revolveType" : RevolveType.FULL});
        }
        {
            var Q0;
            Q0=makeQuery(id+"F25.imprint","IMPRINT",FACE,{"disambiguationData":[TD([[makeQuery(id+"F25.imprint","IMPRINT",EDGE,{"derivedFrom":sQuery(id+"F25.wireOp",EDGE,"E127")}),-1.0]])]});
            var Q1;
            Q1=sQuery(id+"F25.wireOp",EDGE,"E128");
            revolve(context, id + "F36", {"entities" : qUnion([Q0]), "axis" : qUnion([Q1]), "revolveType" : RevolveType.FULL});
        }
        {
            var Q0;
            Q0=qCreatedBy(makeId("Top.planeOp"),FACE);
            var sketch = newSketch(context, id + "F37", { "sketchPlane" : qUnion([Q0])});
            skLineSegment(sketch, "E131", {"start": v(-2.65, 66.85) * mm, "end": v(-2.65, 64.95) * mm});
            skLineSegment(sketch, "E132", {"start": v(-2.02, 64.95) * mm, "end": v(-2.02, 67.09) * mm});
            skLineSegment(sketch, "E133", {"start": v(-4.29, 67.99) * mm, "end": v(-2.92, 67.99) * mm});
            skLineSegment(sketch, "E134", {"start": v(-4.33, 67.18) * mm, "end": v(-3.07, 67.18) * mm});
            skArc(sketch, "E135", {"start": v(-2.65, 64.95) * mm, "mid": v(-2.34, 64.63) * mm, "end": v(-2.02, 64.95) * mm});
            skArc(sketch, "E136", {"start": v(-2.02, 67.09) * mm, "mid": v(-2.29, 67.72) * mm, "end": v(-2.92, 67.99) * mm});
            skArc(sketch, "E137", {"start": v(-4.54, 68.2) * mm, "mid": v(-4.85, 67.6) * mm, "end": v(-4.33, 67.18) * mm});
            skLineSegment(sketch, "E138", {"start": v(-4.54, 68.2) * mm, "end": v(-4.29, 67.99) * mm});
            skArc(sketch, "E139", {"start": v(-2.65, 66.85) * mm, "mid": v(-2.8, 67.09) * mm, "end": v(-3.07, 67.18) * mm});
            skLineSegment(sketch, "E140", {"start": v(-0.98, 67.94) * mm, "end": v(0.9, 67.94) * mm});
            skLineSegment(sketch, "E141", {"start": v(1.31, 67.38) * mm, "end": v(1.31, 64.82) * mm});
            skLineSegment(sketch, "E142", {"start": v(0.87, 66.89) * mm, "end": v(0.87, 64.88) * mm});
            skLineSegment(sketch, "E143", {"start": v(0.57, 67.15) * mm, "end": v(-0.5, 67.15) * mm});
            skArc(sketch, "E144", {"start": v(0.87, 66.89) * mm, "mid": v(0.77, 67.08) * mm, "end": v(0.57, 67.15) * mm});
            skArc(sketch, "E145", {"start": v(1.31, 67.38) * mm, "mid": v(1.2, 67.73) * mm, "end": v(0.9, 67.94) * mm});
            skArc(sketch, "E146", {"start": v(-1.23, 68.21) * mm, "mid": v(-1.47, 67.7) * mm, "end": v(-1.18, 67.2) * mm});
            skLineSegment(sketch, "E147", {"start": v(-1.23, 68.21) * mm, "end": v(-0.98, 67.94) * mm});
            skLineSegment(sketch, "E148", {"start": v(-1.18, 67.2) * mm, "end": v(-0.98, 67.2) * mm});
            skArc(sketch, "E149", {"start": v(-0.98, 67.2) * mm, "mid": v(-1.34, 66.8) * mm, "end": v(-1.46, 66.26) * mm});
            skLineSegment(sketch, "E150", {"start": v(-1.07, 65.65) * mm, "end": v(-1.07, 65.43) * mm});
            skArc(sketch, "E151", {"start": v(-1.07, 65.43) * mm, "mid": v(-1.52, 65.06) * mm, "end": v(-1.07, 64.68) * mm});
            skFitSpline(sketch, "E152", {"points": [v(-1.07, 64.68) * mm, v(-0.72, 64.9) * mm, v(-0.72, 65.58) * mm, v(-0.99, 66.13) * mm, v(-1.07, 66.32) * mm, v(-0.93, 66.68) * mm, v(-0.65, 67.07) * mm, v(-0.5, 67.15) * mm], "startDerivative": vector(2.86, 0.91) * mm, "endDerivative": vector(1.58, 0.57) * mm});
            skFitSpline(sketch, "E153", {"points": [v(0.87, 64.88) * mm, v(1.11, 64.7) * mm, v(1.31, 64.82) * mm], "startDerivative": vector(0.55, -1.2) * mm, "endDerivative": vector(0.5, 0.9) * mm});
            skFitSpline(sketch, "E154", {"points": [v(-1.46, 66.26) * mm, v(-1.07, 65.65) * mm, v(-0.99, 65.9) * mm], "startDerivative": vector(0.76, -1.5) * mm, "endDerivative": vector(0.12, 1) * mm});
            skLineSegment(sketch, "E155", {"start": v(1.95, 68.17) * mm, "end": v(2.17, 67.9) * mm});
            skFitSpline(sketch, "E156", {"points": [v(2.17, 67.9) * mm, v(3.53, 67.9) * mm, v(4.09, 67.65) * mm, v(4.32, 67.26) * mm, v(4.3, 65.66) * mm, v(3.81, 64.83) * mm, v(3.35, 64.7) * mm, v(1.7, 64.7) * mm], "startDerivative": vector(8.76, 0.66) * mm, "endDerivative": vector(-10.12, 0.09) * mm});
            skLineSegment(sketch, "E157", {"start": v(1.7, 64.7) * mm, "end": v(1.96, 65.42) * mm});
            skLineSegment(sketch, "E158", {"start": v(1.96, 65.42) * mm, "end": v(3.26, 65.42) * mm});
            skFitSpline(sketch, "E159", {"points": [v(3.26, 65.42) * mm, v(3.51, 65.42) * mm, v(3.82, 65.74) * mm, v(3.83, 66.7) * mm, v(3.63, 67.08) * mm, v(3.26, 67.15) * mm, v(2.46, 67.16) * mm, v(1.97, 67.2) * mm, v(1.74, 67.58) * mm, v(1.95, 68.17) * mm], "startDerivative": vector(3.24, -0.54) * mm, "endDerivative": vector(2.69, 4.92) * mm});
            skLineSegment(sketch, "E160", {"start": v(22.95, 49.52) * mm, "end": v(22.95, 48.37) * mm});
            skLineSegment(sketch, "E161", {"start": v(23.44, 49.66) * mm, "end": v(23.44, 48.33) * mm});
            skArc(sketch, "E162", {"start": v(22.95, 48.35) * mm, "mid": v(23.19, 48.09) * mm, "end": v(23.44, 48.33) * mm});
            skArc(sketch, "E163", {"start": v(23.44, 49.66) * mm, "mid": v(23.14, 49.77) * mm, "end": v(22.95, 49.52) * mm});
            skLineSegment(sketch, "E164", {"start": v(23.2, 51.4) * mm, "end": v(25.1, 51.4) * mm});
            skLineSegment(sketch, "E165", {"start": v(24.48, 50.57) * mm, "end": v(23.33, 50.57) * mm});
            skLineSegment(sketch, "E166", {"start": v(24.77, 50.22) * mm, "end": v(24.77, 48.46) * mm});
            skLineSegment(sketch, "E167", {"start": v(25.24, 50.18) * mm, "end": v(25.24, 48.42) * mm});
            skArc(sketch, "E168", {"start": v(24.77, 48.46) * mm, "mid": v(24.98, 48.18) * mm, "end": v(25.24, 48.42) * mm});
            skArc(sketch, "E169", {"start": v(24.77, 50.22) * mm, "mid": v(24.7, 50.46) * mm, "end": v(24.48, 50.57) * mm});
            skArc(sketch, "E170", {"start": v(23.01, 51.57) * mm, "mid": v(22.8, 50.95) * mm, "end": v(23.33, 50.57) * mm});
            skLineSegment(sketch, "E171", {"start": v(23.01, 51.57) * mm, "end": v(23.2, 51.4) * mm});
            skFitSpline(sketch, "E172", {"points": [v(25.1, 51.4) * mm, v(25.43, 51.13) * mm, v(25.4, 50.76) * mm, v(25.25, 50.47) * mm, v(25.24, 50.18) * mm], "startDerivative": vector(1.5, -0.87) * mm, "endDerivative": vector(0.17, -1.32) * mm});
            skLineSegment(sketch, "E173", {"start": v(26, 49.95) * mm, "end": v(26, 48.2) * mm});
            skLineSegment(sketch, "E174", {"start": v(26.4, 49.8) * mm, "end": v(26.4, 48.28) * mm});
            skArc(sketch, "E175", {"start": v(26, 48.2) * mm, "mid": v(26.23, 48.06) * mm, "end": v(26.4, 48.28) * mm});
            skLineSegment(sketch, "E176", {"start": v(27.03, 48.86) * mm, "end": v(27.96, 48.86) * mm});
            skLineSegment(sketch, "E177", {"start": v(26.75, 48.11) * mm, "end": v(27.03, 48.86) * mm});
            skLineSegment(sketch, "E178", {"start": v(26.75, 48.11) * mm, "end": v(28.14, 48.11) * mm});
            skFitSpline(sketch, "E179", {"points": [v(26, 49.95) * mm, v(26.49, 50.53) * mm, v(26.4, 50.58) * mm, v(26.13, 50.74) * mm, v(26, 51.12) * mm, v(26.17, 51.52) * mm, v(26.29, 51.59) * mm, v(26.32, 51.46) * mm, v(26.65, 51.38) * mm, v(26.86, 51.24) * mm, v(26.96, 50.87) * mm, v(27.05, 50.85) * mm, v(27.14, 50.86) * mm, v(27.11, 51.32) * mm, v(27.53, 51.35) * mm, v(27.72, 51.24) * mm, v(28.25, 50.55) * mm, v(28.52, 49.95) * mm, v(28.48, 48.43) * mm, v(28.14, 48.11) * mm], "startDerivative": vector(7.32, 16.46) * mm, "endDerivative": vector(-7.6, -6.16) * mm});
            skFitSpline(sketch, "E180", {"points": [v(27.96, 48.86) * mm, v(28.2, 48.96) * mm, v(28.2, 49.68) * mm, v(27.62, 50.5) * mm, v(27.13, 50.6) * mm, v(26.4, 49.8) * mm], "startDerivative": vector(2.16, 0.3) * mm, "endDerivative": vector(-1.57, -3.8) * mm});
            skFitSpline(sketch, "E181", {"points": [v(29.38, 51.35) * mm, v(30.6, 51.3) * mm, v(31.04, 51.19) * mm, v(31.4, 50.84) * mm, v(31.46, 50.21) * mm, v(31.45, 49.18) * mm, v(31.2, 48.58) * mm, v(30.64, 48.12) * mm, v(28.87, 48.04) * mm], "startDerivative": vector(11.68, -1.4) * mm, "endDerivative": vector(-10.94, 0.39) * mm});
            skLineSegment(sketch, "E182", {"start": v(28.87, 48.04) * mm, "end": v(29.14, 48.83) * mm});
            skFitSpline(sketch, "E183", {"points": [v(29.14, 48.83) * mm, v(30.4, 48.83) * mm, v(30.9, 49.02) * mm, v(31.04, 49.5) * mm, v(31.02, 50.21) * mm, v(30.77, 50.6) * mm, v(30.56, 50.66) * mm, v(29.9, 50.64) * mm, v(29.06, 50.8) * mm, v(28.95, 51.2) * mm, v(29.14, 51.61) * mm, v(29.38, 51.35) * mm], "startDerivative": vector(10.18, -0.43) * mm, "endDerivative": vector(4.81, 1.95) * mm});
            skLineSegment(sketch, "E184", {"start": v(32.17, 50.31) * mm, "end": v(32.17, 48.23) * mm});
            skLineSegment(sketch, "E185", {"start": v(32.62, 50.3) * mm, "end": v(32.62, 48.24) * mm});
            skArc(sketch, "E186", {"start": v(32.17, 48.23) * mm, "mid": v(32.4, 48.1) * mm, "end": v(32.62, 48.24) * mm});
            skLineSegment(sketch, "E187", {"start": v(32.4, 51.4) * mm, "end": v(34.16, 51.4) * mm});
            skArc(sketch, "E188", {"start": v(34.68, 51) * mm, "mid": v(34.48, 51.29) * mm, "end": v(34.16, 51.4) * mm});
            skLineSegment(sketch, "E189", {"start": v(34.02, 50.16) * mm, "end": v(34.02, 48.24) * mm});
            skLineSegment(sketch, "E190", {"start": v(34.42, 50.31) * mm, "end": v(34.42, 48.33) * mm});
            skArc(sketch, "E191", {"start": v(34.02, 48.24) * mm, "mid": v(34.26, 48.13) * mm, "end": v(34.42, 48.33) * mm});
            skLineSegment(sketch, "E192", {"start": v(32.92, 50.6) * mm, "end": v(33.68, 50.6) * mm});
            skArc(sketch, "E193", {"start": v(32.22, 51.57) * mm, "mid": v(31.92, 51.07) * mm, "end": v(32.33, 50.65) * mm});
            skFitSpline(sketch, "E194", {"points": [v(32.17, 50.31) * mm, v(32.48, 50.63) * mm, v(32.33, 50.65) * mm], "startDerivative": vector(-0.05, 1.04) * mm, "endDerivative": vector(-0.57, 0) * mm});
            skFitSpline(sketch, "E195", {"points": [v(32.62, 50.3) * mm, v(32.92, 50.6) * mm], "startDerivative": vector(-0.03, 0.83) * mm, "endDerivative": vector(0.63, -0.04) * mm});
            skArc(sketch, "E196", {"start": v(34.02, 50.16) * mm, "mid": v(33.96, 50.46) * mm, "end": v(33.68, 50.6) * mm});
            skFitSpline(sketch, "E197", {"points": [v(34.42, 50.31) * mm, v(34.57, 50.55) * mm, v(34.67, 50.83) * mm, v(34.68, 51) * mm], "startDerivative": vector(0.43, 0.64) * mm, "endDerivative": vector(0, 0.59) * mm});
            skLineSegment(sketch, "E198", {"start": v(32.4, 51.4) * mm, "end": v(32.24, 51.4) * mm});
            skLineSegment(sketch, "E199", {"start": v(32.22, 51.57) * mm, "end": v(32.24, 51.4) * mm});
            skLineSegment(sketch, "E200", {"start": v(-33.53, 49.6) * mm, "end": v(-33.53, 48.34) * mm});
            skLineSegment(sketch, "E201", {"start": v(-33.19, 49.7) * mm, "end": v(-33.19, 48.34) * mm});
            skLineSegment(sketch, "E202", {"start": v(-31.77, 50.4) * mm, "end": v(-31.77, 48.4) * mm});
            skLineSegment(sketch, "E203", {"start": v(-31.4, 50.37) * mm, "end": v(-31.4, 48.4) * mm});
            skArc(sketch, "E204", {"start": v(-31.77, 48.4) * mm, "mid": v(-31.59, 48.21) * mm, "end": v(-31.4, 48.4) * mm});
            skArc(sketch, "E205", {"start": v(-33.53, 48.34) * mm, "mid": v(-33.36, 48.17) * mm, "end": v(-33.19, 48.34) * mm});
            skArc(sketch, "E206", {"start": v(-33.19, 49.7) * mm, "mid": v(-33.4, 49.78) * mm, "end": v(-33.53, 49.6) * mm});
            skFitSpline(sketch, "E207", {"points": [v(-31.4, 50.37) * mm, v(-31.4, 50.5) * mm, v(-31.3, 50.66) * mm, v(-31.21, 51.24) * mm, v(-31.56, 51.37) * mm], "startDerivative": vector(-0.07, 0.9) * mm, "endDerivative": vector(-1.73, -0.16) * mm});
            skLineSegment(sketch, "E208", {"start": v(-31.56, 51.37) * mm, "end": v(-33.43, 51.37) * mm});
            skLineSegment(sketch, "E209", {"start": v(-33.43, 51.37) * mm, "end": v(-33.54, 51.6) * mm});
            skArc(sketch, "E210", {"start": v(-33.54, 51.6) * mm, "mid": v(-33.81, 51.13) * mm, "end": v(-33.54, 50.67) * mm});
            skLineSegment(sketch, "E211", {"start": v(-33.54, 50.67) * mm, "end": v(-32.15, 50.67) * mm});
            skArc(sketch, "E212", {"start": v(-31.77, 50.4) * mm, "mid": v(-31.9, 50.63) * mm, "end": v(-32.15, 50.67) * mm});
            skFitSpline(sketch, "E213", {"points": [v(-29.99, 50.61) * mm, v(-29.82, 50.34) * mm, v(-29.8, 49.3) * mm, v(-29.9, 48.95) * mm, v(-30.62, 48.88) * mm], "startDerivative": vector(1.21, -1.4) * mm, "endDerivative": vector(-3.24, 0.16) * mm});
            skLineSegment(sketch, "E214", {"start": v(-30.62, 48.88) * mm, "end": v(-30.9, 48.13) * mm});
            skLineSegment(sketch, "E215", {"start": v(-30.9, 48.13) * mm, "end": v(-30, 48.13) * mm});
            skFitSpline(sketch, "E216", {"points": [v(-30, 48.13) * mm, v(-29.77, 48.25) * mm, v(-29.56, 48.5) * mm, v(-29.5, 48.67) * mm], "startDerivative": vector(0.72, 0.27) * mm, "endDerivative": vector(0.13, 0.6) * mm});
            skLineSegment(sketch, "E217", {"start": v(-29.5, 48.67) * mm, "end": v(-29.5, 50.98) * mm});
            skArc(sketch, "E218", {"start": v(-29.5, 50.98) * mm, "mid": v(-29.62, 51.25) * mm, "end": v(-29.9, 51.35) * mm});
            skArc(sketch, "E219", {"start": v(-30.34, 51.52) * mm, "mid": v(-30.57, 51.1) * mm, "end": v(-30.33, 50.69) * mm});
            skLineSegment(sketch, "E220", {"start": v(-30.33, 50.69) * mm, "end": v(-29.99, 50.61) * mm});
            skLineSegment(sketch, "E221", {"start": v(-30.34, 51.52) * mm, "end": v(-30.26, 51.4) * mm});
            skLineSegment(sketch, "E222", {"start": v(-30.26, 51.4) * mm, "end": v(-29.9, 51.35) * mm});
            skLineSegment(sketch, "E223", {"start": v(-28.56, 51.41) * mm, "end": v(-28.37, 51.33) * mm});
            skLineSegment(sketch, "E224", {"start": v(-28.37, 51.33) * mm, "end": v(-28.1, 51.33) * mm});
            skPoint(sketch, "E225.6.internal.snap0", {"position": v(-28.47, 51.37) * mm});
            skFitSpline(sketch, "E225", {"points": [v(-28.1, 51.33) * mm, v(-27.93, 51.29) * mm, v(-27.9, 51.16) * mm, v(-27.86, 50.56) * mm, v(-28.1, 50.18) * mm, v(-28.33, 49.92) * mm, v(-28.47, 49.9) * mm, v(-28.41, 50.07) * mm, v(-28.1, 50.46) * mm, v(-28.1, 50.59) * mm, v(-28.16, 50.68) * mm, v(-28.33, 50.72) * mm, v(-28.64, 50.69) * mm, v(-28.81, 50.87) * mm, v(-28.85, 51.19) * mm, v(-28.73, 51.5) * mm, v(-28.63, 51.6) * mm, v(-28.63, 51.41) * mm, v(-28.56, 51.41) * mm], "startDerivative": vector(3.19, -0.87) * mm, "endDerivative": vector(2.83, 1.09) * mm});
            skLineSegment(sketch, "E226", {"start": v(-25.38, 50.44) * mm, "end": v(-25.38, 49.02) * mm});
            skLineSegment(sketch, "E227", {"start": v(-25.55, 48.87) * mm, "end": v(-27.05, 48.87) * mm});
            skLineSegment(sketch, "E228", {"start": v(-27.05, 48.87) * mm, "end": v(-27.37, 48.12) * mm});
            skLineSegment(sketch, "E229", {"start": v(-27.37, 48.12) * mm, "end": v(-24.92, 48.12) * mm});
            skLineSegment(sketch, "E230", {"start": v(-24.92, 48.12) * mm, "end": v(-24.63, 48.87) * mm});
            skLineSegment(sketch, "E231", {"start": v(-24.63, 48.87) * mm, "end": v(-24.93, 48.87) * mm});
            skLineSegment(sketch, "E232", {"start": v(-24.93, 48.87) * mm, "end": v(-24.93, 50.96) * mm});
            skArc(sketch, "E233", {"start": v(-24.93, 50.96) * mm, "mid": v(-25.06, 51.27) * mm, "end": v(-25.38, 51.38) * mm});
            skLineSegment(sketch, "E234", {"start": v(-25.38, 51.38) * mm, "end": v(-27.07, 51.38) * mm});
            skLineSegment(sketch, "E235", {"start": v(-27.07, 51.38) * mm, "end": v(-27.07, 51.6) * mm});
            skArc(sketch, "E236", {"start": v(-27.07, 51.6) * mm, "mid": v(-27.38, 51.12) * mm, "end": v(-27.07, 50.65) * mm});
            skLineSegment(sketch, "E237", {"start": v(-27.07, 50.65) * mm, "end": v(-25.74, 50.65) * mm});
            skArc(sketch, "E238", {"start": v(-25.38, 50.44) * mm, "mid": v(-25.53, 50.6) * mm, "end": v(-25.74, 50.65) * mm});
            skArc(sketch, "E239", {"start": v(-25.55, 48.87) * mm, "mid": v(-25.43, 48.9) * mm, "end": v(-25.38, 49.02) * mm});
            skLineSegment(sketch, "E240", {"start": v(-94.15, 45.97) * mm, "end": v(-94.15, 44.06) * mm});
            skLineSegment(sketch, "E241", {"start": v(-93.52, 44.06) * mm, "end": v(-93.52, 46.2) * mm});
            skLineSegment(sketch, "E242", {"start": v(-95.79, 47.1) * mm, "end": v(-94.42, 47.1) * mm});
            skLineSegment(sketch, "E243", {"start": v(-95.82, 46.3) * mm, "end": v(-94.57, 46.3) * mm});
            skArc(sketch, "E244", {"start": v(-94.15, 44.06) * mm, "mid": v(-93.84, 43.75) * mm, "end": v(-93.52, 44.06) * mm});
            skArc(sketch, "E245", {"start": v(-93.52, 46.2) * mm, "mid": v(-93.78, 46.84) * mm, "end": v(-94.42, 47.1) * mm});
            skArc(sketch, "E246", {"start": v(-96.04, 47.32) * mm, "mid": v(-96.35, 46.72) * mm, "end": v(-95.82, 46.3) * mm});
            skLineSegment(sketch, "E247", {"start": v(-96.04, 47.32) * mm, "end": v(-95.79, 47.1) * mm});
            skArc(sketch, "E248", {"start": v(-94.15, 45.97) * mm, "mid": v(-94.3, 46.2) * mm, "end": v(-94.57, 46.3) * mm});
            skLineSegment(sketch, "E249", {"start": v(-92.48, 47.06) * mm, "end": v(-90.6, 47.06) * mm});
            skLineSegment(sketch, "E250", {"start": v(-90.19, 46.5) * mm, "end": v(-90.19, 43.93) * mm});
            skLineSegment(sketch, "E251", {"start": v(-90.63, 46) * mm, "end": v(-90.63, 44) * mm});
            skLineSegment(sketch, "E252", {"start": v(-90.93, 46.27) * mm, "end": v(-92, 46.27) * mm});
            skArc(sketch, "E253", {"start": v(-90.63, 46) * mm, "mid": v(-90.73, 46.2) * mm, "end": v(-90.93, 46.27) * mm});
            skArc(sketch, "E254", {"start": v(-90.19, 46.5) * mm, "mid": v(-90.3, 46.85) * mm, "end": v(-90.6, 47.06) * mm});
            skArc(sketch, "E255", {"start": v(-92.73, 47.33) * mm, "mid": v(-92.97, 46.81) * mm, "end": v(-92.68, 46.32) * mm});
            skLineSegment(sketch, "E256", {"start": v(-92.73, 47.33) * mm, "end": v(-92.48, 47.06) * mm});
            skLineSegment(sketch, "E257", {"start": v(-92.68, 46.32) * mm, "end": v(-92.48, 46.32) * mm});
            skArc(sketch, "E258", {"start": v(-92.48, 46.32) * mm, "mid": v(-92.84, 45.9) * mm, "end": v(-92.96, 45.38) * mm});
            skLineSegment(sketch, "E259", {"start": v(-92.57, 44.76) * mm, "end": v(-92.57, 44.54) * mm});
            skArc(sketch, "E260", {"start": v(-92.57, 44.54) * mm, "mid": v(-93.02, 44.17) * mm, "end": v(-92.57, 43.8) * mm});
            skFitSpline(sketch, "E261", {"points": [v(-92.57, 43.8) * mm, v(-92.22, 44) * mm, v(-92.22, 44.7) * mm, v(-92.49, 45.25) * mm, v(-92.57, 45.44) * mm, v(-92.43, 45.8) * mm, v(-92.15, 46.19) * mm, v(-92, 46.27) * mm], "startDerivative": vector(2.86, 0.91) * mm, "endDerivative": vector(1.58, 0.57) * mm});
            skFitSpline(sketch, "E262", {"points": [v(-90.63, 44) * mm, v(-90.39, 43.8) * mm, v(-90.19, 43.93) * mm], "startDerivative": vector(0.55, -1.2) * mm, "endDerivative": vector(0.5, 0.9) * mm});
            skFitSpline(sketch, "E263", {"points": [v(-92.96, 45.38) * mm, v(-92.57, 44.76) * mm, v(-92.49, 45.02) * mm], "startDerivative": vector(0.76, -1.5) * mm, "endDerivative": vector(0.12, 1) * mm});
            skLineSegment(sketch, "E264", {"start": v(-89.55, 47.29) * mm, "end": v(-89.33, 47.03) * mm});
            skFitSpline(sketch, "E265", {"points": [v(-89.33, 47.03) * mm, v(-87.97, 47.03) * mm, v(-87.41, 46.76) * mm, v(-87.18, 46.37) * mm, v(-87.2, 44.77) * mm, v(-87.69, 43.95) * mm, v(-88.14, 43.81) * mm, v(-89.8, 43.82) * mm], "startDerivative": vector(8.76, 0.66) * mm, "endDerivative": vector(-10.12, 0.09) * mm});
            skLineSegment(sketch, "E266", {"start": v(-89.8, 43.82) * mm, "end": v(-89.54, 44.53) * mm});
            skLineSegment(sketch, "E267", {"start": v(-89.54, 44.53) * mm, "end": v(-88.24, 44.53) * mm});
            skFitSpline(sketch, "E268", {"points": [v(-88.24, 44.53) * mm, v(-87.99, 44.53) * mm, v(-87.68, 44.86) * mm, v(-87.67, 45.82) * mm, v(-87.87, 46.2) * mm, v(-88.24, 46.27) * mm, v(-89.04, 46.28) * mm, v(-89.53, 46.32) * mm, v(-89.76, 46.7) * mm, v(-89.55, 47.29) * mm], "startDerivative": vector(3.24, -0.54) * mm, "endDerivative": vector(2.69, 4.92) * mm});
            skLineSegment(sketch, "E269", {"start": v(-68.55, 28.63) * mm, "end": v(-68.55, 27.49) * mm});
            skLineSegment(sketch, "E270", {"start": v(-68.06, 28.78) * mm, "end": v(-68.06, 27.45) * mm});
            skArc(sketch, "E271", {"start": v(-68.55, 27.47) * mm, "mid": v(-68.31, 27.2) * mm, "end": v(-68.06, 27.45) * mm});
            skArc(sketch, "E272", {"start": v(-68.06, 28.78) * mm, "mid": v(-68.36, 28.89) * mm, "end": v(-68.55, 28.63) * mm});
            skLineSegment(sketch, "E273", {"start": v(-68.3, 30.52) * mm, "end": v(-66.4, 30.52) * mm});
            skLineSegment(sketch, "E274", {"start": v(-67.02, 29.69) * mm, "end": v(-68.17, 29.69) * mm});
            skLineSegment(sketch, "E275", {"start": v(-66.73, 29.34) * mm, "end": v(-66.73, 27.58) * mm});
            skLineSegment(sketch, "E276", {"start": v(-66.26, 29.3) * mm, "end": v(-66.26, 27.54) * mm});
            skArc(sketch, "E277", {"start": v(-66.73, 27.58) * mm, "mid": v(-66.52, 27.3) * mm, "end": v(-66.26, 27.54) * mm});
            skArc(sketch, "E278", {"start": v(-66.73, 29.34) * mm, "mid": v(-66.8, 29.58) * mm, "end": v(-67.02, 29.69) * mm});
            skArc(sketch, "E279", {"start": v(-68.49, 30.68) * mm, "mid": v(-68.7, 30.07) * mm, "end": v(-68.17, 29.69) * mm});
            skLineSegment(sketch, "E280", {"start": v(-68.49, 30.68) * mm, "end": v(-68.3, 30.52) * mm});
            skFitSpline(sketch, "E281", {"points": [v(-66.4, 30.52) * mm, v(-66.07, 30.24) * mm, v(-66.1, 29.88) * mm, v(-66.25, 29.59) * mm, v(-66.26, 29.3) * mm], "startDerivative": vector(1.5, -0.87) * mm, "endDerivative": vector(0.17, -1.32) * mm});
            skLineSegment(sketch, "E282", {"start": v(-65.5, 29.07) * mm, "end": v(-65.5, 27.32) * mm});
            skLineSegment(sketch, "E283", {"start": v(-65.1, 28.92) * mm, "end": v(-65.1, 27.4) * mm});
            skArc(sketch, "E284", {"start": v(-65.5, 27.32) * mm, "mid": v(-65.27, 27.18) * mm, "end": v(-65.1, 27.4) * mm});
            skLineSegment(sketch, "E285", {"start": v(-64.47, 27.98) * mm, "end": v(-63.54, 27.98) * mm});
            skLineSegment(sketch, "E286", {"start": v(-64.75, 27.23) * mm, "end": v(-64.47, 27.98) * mm});
            skLineSegment(sketch, "E287", {"start": v(-64.75, 27.23) * mm, "end": v(-63.36, 27.23) * mm});
            skFitSpline(sketch, "E288", {"points": [v(-65.5, 29.07) * mm, v(-65.01, 29.64) * mm, v(-65.1, 29.7) * mm, v(-65.37, 29.85) * mm, v(-65.5, 30.24) * mm, v(-65.33, 30.64) * mm, v(-65.21, 30.7) * mm, v(-65.18, 30.58) * mm, v(-64.85, 30.5) * mm, v(-64.64, 30.36) * mm, v(-64.54, 29.98) * mm, v(-64.45, 29.96) * mm, v(-64.36, 29.97) * mm, v(-64.38, 30.44) * mm, v(-63.97, 30.47) * mm, v(-63.78, 30.36) * mm, v(-63.25, 29.66) * mm, v(-62.98, 29.07) * mm, v(-63.02, 27.54) * mm, v(-63.36, 27.23) * mm], "startDerivative": vector(7.32, 16.46) * mm, "endDerivative": vector(-7.6, -6.16) * mm});
            skFitSpline(sketch, "E289", {"points": [v(-63.54, 27.98) * mm, v(-63.3, 28.08) * mm, v(-63.3, 28.8) * mm, v(-63.88, 29.6) * mm, v(-64.37, 29.7) * mm, v(-65.1, 28.92) * mm], "startDerivative": vector(2.16, 0.3) * mm, "endDerivative": vector(-1.57, -3.8) * mm});
            skFitSpline(sketch, "E290", {"points": [v(-62.12, 30.47) * mm, v(-60.9, 30.42) * mm, v(-60.46, 30.3) * mm, v(-60.1, 29.96) * mm, v(-60.04, 29.33) * mm, v(-60.05, 28.3) * mm, v(-60.3, 27.7) * mm, v(-60.86, 27.24) * mm, v(-62.63, 27.16) * mm], "startDerivative": vector(11.68, -1.4) * mm, "endDerivative": vector(-10.94, 0.39) * mm});
            skLineSegment(sketch, "E291", {"start": v(-62.63, 27.16) * mm, "end": v(-62.36, 27.95) * mm});
            skFitSpline(sketch, "E292", {"points": [v(-62.36, 27.95) * mm, v(-61.1, 27.95) * mm, v(-60.6, 28.13) * mm, v(-60.46, 28.61) * mm, v(-60.48, 29.33) * mm, v(-60.73, 29.7) * mm, v(-60.94, 29.78) * mm, v(-61.6, 29.76) * mm, v(-62.44, 29.92) * mm, v(-62.55, 30.33) * mm, v(-62.36, 30.73) * mm, v(-62.12, 30.47) * mm], "startDerivative": vector(10.18, -0.43) * mm, "endDerivative": vector(4.81, 1.95) * mm});
            skLineSegment(sketch, "E293", {"start": v(-59.33, 29.43) * mm, "end": v(-59.33, 27.34) * mm});
            skLineSegment(sketch, "E294", {"start": v(-58.88, 29.4) * mm, "end": v(-58.88, 27.35) * mm});
            skArc(sketch, "E295", {"start": v(-59.33, 27.34) * mm, "mid": v(-59.1, 27.2) * mm, "end": v(-58.88, 27.35) * mm});
            skLineSegment(sketch, "E296", {"start": v(-59.1, 30.51) * mm, "end": v(-57.34, 30.51) * mm});
            skArc(sketch, "E297", {"start": v(-56.82, 30.12) * mm, "mid": v(-57.02, 30.4) * mm, "end": v(-57.34, 30.51) * mm});
            skLineSegment(sketch, "E298", {"start": v(-57.48, 29.27) * mm, "end": v(-57.48, 27.35) * mm});
            skLineSegment(sketch, "E299", {"start": v(-57.08, 29.43) * mm, "end": v(-57.08, 27.45) * mm});
            skArc(sketch, "E300", {"start": v(-57.48, 27.35) * mm, "mid": v(-57.24, 27.24) * mm, "end": v(-57.08, 27.45) * mm});
            skLineSegment(sketch, "E301", {"start": v(-58.58, 29.7) * mm, "end": v(-57.82, 29.7) * mm});
            skArc(sketch, "E302", {"start": v(-59.28, 30.69) * mm, "mid": v(-59.58, 30.19) * mm, "end": v(-59.17, 29.77) * mm});
            skFitSpline(sketch, "E303", {"points": [v(-59.33, 29.43) * mm, v(-59.02, 29.74) * mm, v(-59.17, 29.77) * mm], "startDerivative": vector(-0.05, 1.04) * mm, "endDerivative": vector(-0.57, 0) * mm});
            skFitSpline(sketch, "E304", {"points": [v(-58.88, 29.4) * mm, v(-58.58, 29.7) * mm], "startDerivative": vector(-0.03, 0.83) * mm, "endDerivative": vector(0.63, -0.04) * mm});
            skArc(sketch, "E305", {"start": v(-57.48, 29.27) * mm, "mid": v(-57.54, 29.57) * mm, "end": v(-57.82, 29.7) * mm});
            skFitSpline(sketch, "E306", {"points": [v(-57.08, 29.43) * mm, v(-56.93, 29.67) * mm, v(-56.83, 29.94) * mm, v(-56.82, 30.12) * mm], "startDerivative": vector(0.43, 0.64) * mm, "endDerivative": vector(0, 0.59) * mm});
            skLineSegment(sketch, "E307", {"start": v(-59.1, 30.51) * mm, "end": v(-59.26, 30.51) * mm});
            skLineSegment(sketch, "E308", {"start": v(-59.28, 30.69) * mm, "end": v(-59.26, 30.51) * mm});
            skLineSegment(sketch, "E309", {"start": v(-125.03, 28.72) * mm, "end": v(-125.03, 27.46) * mm});
            skLineSegment(sketch, "E310", {"start": v(-124.69, 28.8) * mm, "end": v(-124.69, 27.46) * mm});
            skLineSegment(sketch, "E311", {"start": v(-123.27, 29.52) * mm, "end": v(-123.27, 27.51) * mm});
            skLineSegment(sketch, "E312", {"start": v(-122.9, 29.49) * mm, "end": v(-122.9, 27.51) * mm});
            skArc(sketch, "E313", {"start": v(-123.27, 27.51) * mm, "mid": v(-123.09, 27.33) * mm, "end": v(-122.9, 27.51) * mm});
            skArc(sketch, "E314", {"start": v(-125.03, 27.46) * mm, "mid": v(-124.86, 27.29) * mm, "end": v(-124.69, 27.46) * mm});
            skArc(sketch, "E315", {"start": v(-124.69, 28.8) * mm, "mid": v(-124.9, 28.9) * mm, "end": v(-125.03, 28.72) * mm});
            skFitSpline(sketch, "E316", {"points": [v(-122.9, 29.49) * mm, v(-122.9, 29.62) * mm, v(-122.8, 29.78) * mm, v(-122.71, 30.36) * mm, v(-123.06, 30.5) * mm], "startDerivative": vector(-0.07, 0.9) * mm, "endDerivative": vector(-1.73, -0.16) * mm});
            skLineSegment(sketch, "E317", {"start": v(-123.06, 30.5) * mm, "end": v(-124.93, 30.5) * mm});
            skLineSegment(sketch, "E318", {"start": v(-124.93, 30.5) * mm, "end": v(-125.04, 30.71) * mm});
            skArc(sketch, "E319", {"start": v(-125.04, 30.71) * mm, "mid": v(-125.31, 30.25) * mm, "end": v(-125.04, 29.79) * mm});
            skLineSegment(sketch, "E320", {"start": v(-125.04, 29.79) * mm, "end": v(-123.65, 29.79) * mm});
            skArc(sketch, "E321", {"start": v(-123.27, 29.52) * mm, "mid": v(-123.4, 29.75) * mm, "end": v(-123.65, 29.79) * mm});
            skFitSpline(sketch, "E322", {"points": [v(-121.49, 29.73) * mm, v(-121.32, 29.45) * mm, v(-121.3, 28.41) * mm, v(-121.4, 28.07) * mm, v(-122.12, 28) * mm], "startDerivative": vector(1.21, -1.4) * mm, "endDerivative": vector(-3.24, 0.16) * mm});
            skLineSegment(sketch, "E323", {"start": v(-122.12, 28) * mm, "end": v(-122.4, 27.24) * mm});
            skLineSegment(sketch, "E324", {"start": v(-122.4, 27.24) * mm, "end": v(-121.5, 27.24) * mm});
            skFitSpline(sketch, "E325", {"points": [v(-121.5, 27.24) * mm, v(-121.27, 27.36) * mm, v(-121.06, 27.61) * mm, v(-121, 27.79) * mm], "startDerivative": vector(0.72, 0.27) * mm, "endDerivative": vector(0.13, 0.6) * mm});
            skLineSegment(sketch, "E326", {"start": v(-121, 27.79) * mm, "end": v(-121, 30.1) * mm});
            skArc(sketch, "E327", {"start": v(-121, 30.1) * mm, "mid": v(-121.12, 30.37) * mm, "end": v(-121.4, 30.47) * mm});
            skArc(sketch, "E328", {"start": v(-121.84, 30.64) * mm, "mid": v(-122.07, 30.22) * mm, "end": v(-121.83, 29.8) * mm});
            skLineSegment(sketch, "E329", {"start": v(-121.83, 29.8) * mm, "end": v(-121.49, 29.73) * mm});
            skLineSegment(sketch, "E330", {"start": v(-121.84, 30.64) * mm, "end": v(-121.76, 30.52) * mm});
            skLineSegment(sketch, "E331", {"start": v(-121.76, 30.52) * mm, "end": v(-121.4, 30.47) * mm});
            skLineSegment(sketch, "E332", {"start": v(-120.06, 30.53) * mm, "end": v(-119.87, 30.45) * mm});
            skLineSegment(sketch, "E333", {"start": v(-119.87, 30.45) * mm, "end": v(-119.6, 30.45) * mm});
            skPoint(sketch, "E334.6.internal.snap0", {"position": v(-119.97, 30.5) * mm});
            skFitSpline(sketch, "E334", {"points": [v(-119.6, 30.45) * mm, v(-119.43, 30.4) * mm, v(-119.4, 30.28) * mm, v(-119.36, 29.68) * mm, v(-119.6, 29.3) * mm, v(-119.83, 29.04) * mm, v(-119.97, 29.02) * mm, v(-119.91, 29.19) * mm, v(-119.6, 29.58) * mm, v(-119.6, 29.7) * mm, v(-119.66, 29.8) * mm, v(-119.83, 29.83) * mm, v(-120.14, 29.8) * mm, v(-120.31, 29.98) * mm, v(-120.35, 30.3) * mm, v(-120.23, 30.62) * mm, v(-120.13, 30.71) * mm, v(-120.13, 30.53) * mm, v(-120.06, 30.53) * mm], "startDerivative": vector(3.19, -0.87) * mm, "endDerivative": vector(2.83, 1.09) * mm});
            skLineSegment(sketch, "E335", {"start": v(-116.88, 29.55) * mm, "end": v(-116.88, 28.13) * mm});
            skLineSegment(sketch, "E336", {"start": v(-117.05, 27.98) * mm, "end": v(-118.55, 27.98) * mm});
            skLineSegment(sketch, "E337", {"start": v(-118.55, 27.98) * mm, "end": v(-118.87, 27.24) * mm});
            skLineSegment(sketch, "E338", {"start": v(-118.87, 27.24) * mm, "end": v(-116.42, 27.24) * mm});
            skLineSegment(sketch, "E339", {"start": v(-116.42, 27.24) * mm, "end": v(-116.13, 28) * mm});
            skLineSegment(sketch, "E340", {"start": v(-116.13, 28) * mm, "end": v(-116.43, 28) * mm});
            skLineSegment(sketch, "E341", {"start": v(-116.43, 28) * mm, "end": v(-116.43, 30.07) * mm});
            skArc(sketch, "E342", {"start": v(-116.43, 30.07) * mm, "mid": v(-116.56, 30.38) * mm, "end": v(-116.88, 30.5) * mm});
            skLineSegment(sketch, "E343", {"start": v(-116.88, 30.5) * mm, "end": v(-118.57, 30.5) * mm});
            skLineSegment(sketch, "E344", {"start": v(-118.57, 30.5) * mm, "end": v(-118.57, 30.71) * mm});
            skArc(sketch, "E345", {"start": v(-118.57, 30.71) * mm, "mid": v(-118.88, 30.24) * mm, "end": v(-118.57, 29.77) * mm});
            skLineSegment(sketch, "E346", {"start": v(-118.57, 29.77) * mm, "end": v(-117.24, 29.77) * mm});
            skArc(sketch, "E347", {"start": v(-116.88, 29.55) * mm, "mid": v(-117.03, 29.71) * mm, "end": v(-117.24, 29.77) * mm});
            skArc(sketch, "E348", {"start": v(-117.05, 27.98) * mm, "mid": v(-116.93, 28.02) * mm, "end": v(-116.88, 28.13) * mm});
            skLineSegment(sketch, "E349", {"start": v(29.9, 16.86) * mm, "end": v(29.9, 14.77) * mm});
            skLineSegment(sketch, "E350", {"start": v(30.36, 16.84) * mm, "end": v(30.36, 14.78) * mm});
            skArc(sketch, "E351", {"start": v(29.9, 14.77) * mm, "mid": v(30.13, 14.64) * mm, "end": v(30.36, 14.78) * mm});
            skLineSegment(sketch, "E352", {"start": v(30.14, 17.95) * mm, "end": v(31.9, 17.95) * mm});
            skArc(sketch, "E353", {"start": v(32.42, 17.55) * mm, "mid": v(32.22, 17.84) * mm, "end": v(31.9, 17.95) * mm});
            skLineSegment(sketch, "E354", {"start": v(31.76, 16.7) * mm, "end": v(31.76, 14.78) * mm});
            skLineSegment(sketch, "E355", {"start": v(32.16, 16.86) * mm, "end": v(32.16, 14.88) * mm});
            skArc(sketch, "E356", {"start": v(31.76, 14.78) * mm, "mid": v(32, 14.68) * mm, "end": v(32.16, 14.88) * mm});
            skLineSegment(sketch, "E357", {"start": v(30.66, 17.14) * mm, "end": v(31.42, 17.14) * mm});
            skArc(sketch, "E358", {"start": v(29.96, 18.12) * mm, "mid": v(29.66, 17.62) * mm, "end": v(30.07, 17.2) * mm});
            skFitSpline(sketch, "E359", {"points": [v(29.9, 16.86) * mm, v(30.22, 17.18) * mm, v(30.07, 17.2) * mm], "startDerivative": vector(-0.05, 1.04) * mm, "endDerivative": vector(-0.57, 0) * mm});
            skFitSpline(sketch, "E360", {"points": [v(30.36, 16.84) * mm, v(30.66, 17.14) * mm], "startDerivative": vector(-0.03, 0.83) * mm, "endDerivative": vector(0.63, -0.04) * mm});
            skArc(sketch, "E361", {"start": v(31.76, 16.7) * mm, "mid": v(31.7, 17) * mm, "end": v(31.42, 17.14) * mm});
            skFitSpline(sketch, "E362", {"points": [v(32.16, 16.86) * mm, v(32.3, 17.1) * mm, v(32.4, 17.38) * mm, v(32.42, 17.55) * mm], "startDerivative": vector(0.43, 0.64) * mm, "endDerivative": vector(0, 0.59) * mm});
            skLineSegment(sketch, "E363", {"start": v(30.14, 17.95) * mm, "end": v(29.98, 17.94) * mm});
            skLineSegment(sketch, "E364", {"start": v(29.96, 18.12) * mm, "end": v(29.98, 17.94) * mm});
            skFitSpline(sketch, "E365", {"points": [v(24.1, 18.14) * mm, v(23.93, 17.96) * mm, v(23.83, 17.7) * mm, v(23.92, 17.32) * mm, v(24.25, 17.15) * mm], "startDerivative": vector(-0.82, -0.75) * mm, "endDerivative": vector(1.44, -0.43) * mm});
            skLineSegment(sketch, "E366", {"start": v(24.25, 17.15) * mm, "end": v(25.66, 17.15) * mm});
            skArc(sketch, "E367", {"start": v(25.66, 16.85) * mm, "mid": v(25.76, 17) * mm, "end": v(25.66, 17.15) * mm});
            skLineSegment(sketch, "E368", {"start": v(24.1, 18.14) * mm, "end": v(24.16, 17.88) * mm});
            skLineSegment(sketch, "E369", {"start": v(24.16, 17.88) * mm, "end": v(26, 17.88) * mm});
            skFitSpline(sketch, "E370", {"points": [v(26, 17.88) * mm, v(26.18, 17.77) * mm, v(26.27, 17.59) * mm, v(26.22, 17.29) * mm, v(26.08, 16.9) * mm, v(26.04, 16.8) * mm], "startDerivative": vector(1.07, -0.48) * mm, "endDerivative": vector(-0.25, -0.6) * mm});
            skLineSegment(sketch, "E371", {"start": v(26.05, 16.83) * mm, "end": v(26.05, 14.8) * mm});
            skLineSegment(sketch, "E372", {"start": v(25.66, 16.85) * mm, "end": v(25.66, 14.79) * mm});
            skArc(sketch, "E373", {"start": v(25.66, 14.79) * mm, "mid": v(25.86, 14.69) * mm, "end": v(26.05, 14.8) * mm});
            skFitSpline(sketch, "E374", {"points": [v(27.22, 16.64) * mm, v(27.15, 16.33) * mm, v(27.17, 15.8) * mm, v(27.43, 15.45) * mm, v(27.81, 15.36) * mm, v(28.42, 15.34) * mm, v(28.71, 15.52) * mm, v(28.95, 15.76) * mm, v(29.03, 16.4) * mm], "startDerivative": vector(-0.8, -1.97) * mm, "endDerivative": vector(-0.5, 4.83) * mm});
            skFitSpline(sketch, "E375", {"points": [v(27.22, 16.64) * mm, v(27.7, 17.16) * mm, v(28.12, 17.18) * mm, v(28.62, 17.15) * mm, v(28.87, 16.93) * mm, v(28.97, 16.77) * mm, v(29.03, 16.4) * mm], "startDerivative": vector(1.94, 2.99) * mm, "endDerivative": vector(0.28, -2.6) * mm});
            skFitSpline(sketch, "E376", {"points": [v(27.33, 17.12) * mm, v(26.9, 16.63) * mm, v(26.85, 15.37) * mm, v(26.98, 15.15) * mm, v(27.3, 14.84) * mm, v(27.54, 14.66) * mm, v(28.61, 14.64) * mm, v(29.05, 14.92) * mm, v(29.29, 15.22) * mm, v(29.33, 15.59) * mm], "startDerivative": vector(-4.1, -2.84) * mm, "endDerivative": vector(-0.04, 4.23) * mm});
            skLineSegment(sketch, "E377", {"start": v(29.33, 15.59) * mm, "end": v(29.33, 17.14) * mm});
            skFitSpline(sketch, "E378", {"points": [v(29.33, 17.14) * mm, v(29.24, 17.5) * mm, v(28.91, 17.73) * mm, v(28.59, 17.87) * mm], "startDerivative": vector(-0.13, 1.18) * mm, "endDerivative": vector(-0.97, 0.42) * mm});
            skLineSegment(sketch, "E379", {"start": v(28.59, 17.87) * mm, "end": v(27.22, 17.87) * mm});
            skLineSegment(sketch, "E380", {"start": v(27.22, 17.87) * mm, "end": v(27.04, 18.1) * mm});
            skArc(sketch, "E381", {"start": v(27.05, 18.13) * mm, "mid": v(26.77, 17.62) * mm, "end": v(27.1, 17.15) * mm});
            skLineSegment(sketch, "E382", {"start": v(27.1, 17.15) * mm, "end": v(27.33, 17.12) * mm});
            skLineSegment(sketch, "E383", {"start": v(-34.87, 16.3) * mm, "end": v(-34.87, 14.96) * mm});
            skLineSegment(sketch, "E384", {"start": v(-34.55, 16.3) * mm, "end": v(-34.55, 14.92) * mm});
            skLineSegment(sketch, "E385", {"start": v(-34.75, 18) * mm, "end": v(-32.86, 18) * mm});
            skLineSegment(sketch, "E386", {"start": v(-33.38, 17.33) * mm, "end": v(-34.47, 17.33) * mm});
            skLineSegment(sketch, "E387", {"start": v(-33.1, 16.97) * mm, "end": v(-33.1, 14.92) * mm});
            skLineSegment(sketch, "E388", {"start": v(-32.64, 16.77) * mm, "end": v(-32.64, 15.03) * mm});
            skArc(sketch, "E389", {"start": v(-33.1, 14.92) * mm, "mid": v(-32.82, 14.8) * mm, "end": v(-32.64, 15.03) * mm});
            skArc(sketch, "E390", {"start": v(-33.1, 16.97) * mm, "mid": v(-33.15, 17.22) * mm, "end": v(-33.38, 17.33) * mm});
            skArc(sketch, "E391", {"start": v(-34.95, 18.15) * mm, "mid": v(-34.94, 17.6) * mm, "end": v(-34.47, 17.33) * mm});
            skLineSegment(sketch, "E392", {"start": v(-34.95, 18.15) * mm, "end": v(-34.75, 18) * mm});
            skFitSpline(sketch, "E393", {"points": [v(-32.86, 18) * mm, v(-32.55, 18) * mm, v(-32.47, 17.86) * mm, v(-32.46, 17.53) * mm, v(-32.63, 17.23) * mm, v(-32.64, 16.77) * mm], "startDerivative": vector(1.86, 0.24) * mm, "endDerivative": vector(0.24, -2.06) * mm});
            skArc(sketch, "E394", {"start": v(-34.55, 16.3) * mm, "mid": v(-34.72, 16.45) * mm, "end": v(-34.87, 16.3) * mm});
            skArc(sketch, "E395", {"start": v(-34.87, 14.96) * mm, "mid": v(-34.73, 14.76) * mm, "end": v(-34.55, 14.92) * mm});
            skLineSegment(sketch, "E396", {"start": v(-29.98, 16.93) * mm, "end": v(-29.98, 15.03) * mm});
            skLineSegment(sketch, "E397", {"start": v(-29.53, 15.03) * mm, "end": v(-29.52, 17.17) * mm});
            skLineSegment(sketch, "E398", {"start": v(-31.61, 18.07) * mm, "end": v(-30.25, 18.07) * mm});
            skLineSegment(sketch, "E399", {"start": v(-31.65, 17.26) * mm, "end": v(-30.4, 17.26) * mm});
            skArc(sketch, "E400", {"start": v(-31.87, 18.28) * mm, "mid": v(-32.17, 17.68) * mm, "end": v(-31.65, 17.26) * mm});
            skLineSegment(sketch, "E401", {"start": v(-31.87, 18.28) * mm, "end": v(-31.61, 18.07) * mm});
            skArc(sketch, "E402", {"start": v(-29.98, 16.93) * mm, "mid": v(-30.13, 17.17) * mm, "end": v(-30.4, 17.26) * mm});
            skArc(sketch, "E403", {"start": v(-29.98, 15.03) * mm, "mid": v(-29.75, 14.8) * mm, "end": v(-29.53, 15.03) * mm});
            skArc(sketch, "E404", {"start": v(-29.52, 17.17) * mm, "mid": v(-29.73, 17.75) * mm, "end": v(-30.25, 18.08) * mm});
            skSolve(sketch);
        }
        {
            var Q0;
            Q0 = qSketchRegion(id + "F37", true);
            extrude(context, id + "F38", {"entities" : qUnion([Q0]), "depth" : 25 * mm, "offsetDistance" : 25 * mm});
        }
    });
